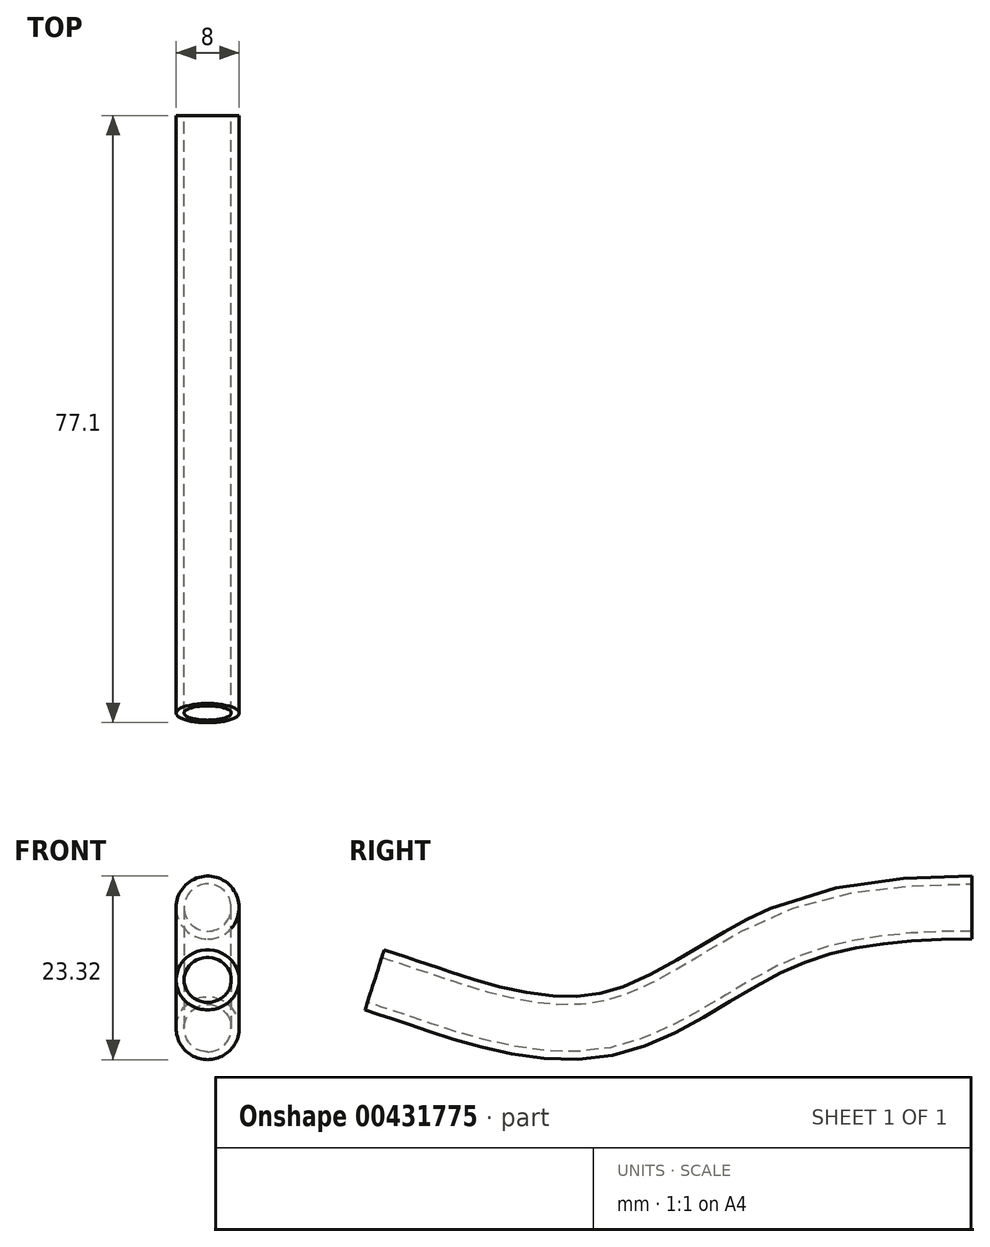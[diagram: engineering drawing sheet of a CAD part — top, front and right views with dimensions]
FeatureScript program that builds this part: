
annotation { "Feature Type Name" : "Feature", "Feature Type Description" : "" }
export const myFeature = defineFeature(function(context is Context, id is Id, definition is map)
    precondition{}
    {
        {
            var Q0;
            Q0=qCreatedBy(makeId("Front.planeOp"),FACE);
            var sketch = newSketch(context, id + "F0", { "sketchPlane" : qUnion([Q0])});
            skCircle(sketch, "E0", {"center": v(0, 0) * mm, "radius": 4 * mm});
            skCircle(sketch, "E1", {"center": v(0, 0) * mm, "radius": 3 * mm});
            skSolve(sketch);
        }
        {
            var Q0;
            Q0=qCreatedBy(makeId("Right.planeOp"),FACE);
            var sketch = newSketch(context, id + "F1", { "sketchPlane" : qUnion([Q0])});
            skFitSpline(sketch, "E2", {"points": [v(0, 0) * mm, v(-24.76, -4.1) * mm, v(-47.3, -15) * mm, v(-68.62, -11.6) * mm, v(-75.89, -9.19) * mm], "startDerivative": vector(-94.03, 0) * mm, "endDerivative": vector(-38.58, 12.3) * mm});
            skSolve(sketch);
        }
        {
            var Q0;
            Q0=makeQuery(id+"F0.imprint","IMPRINT",FACE,{"disambiguationData":[TD([[makeQuery(id+"F0.imprint","IMPRINT",EDGE,{"derivedFrom":sQuery(id+"F0.wireOp",EDGE,"E0")}),1.0]])]});
            var Q1;
            Q1=sQuery(id+"F1.wireOp",EDGE,"E2");
            sweep(context, id + "F2", {"profiles" : qUnion([Q0]), "path" : qUnion([Q1])});
        }
    });
